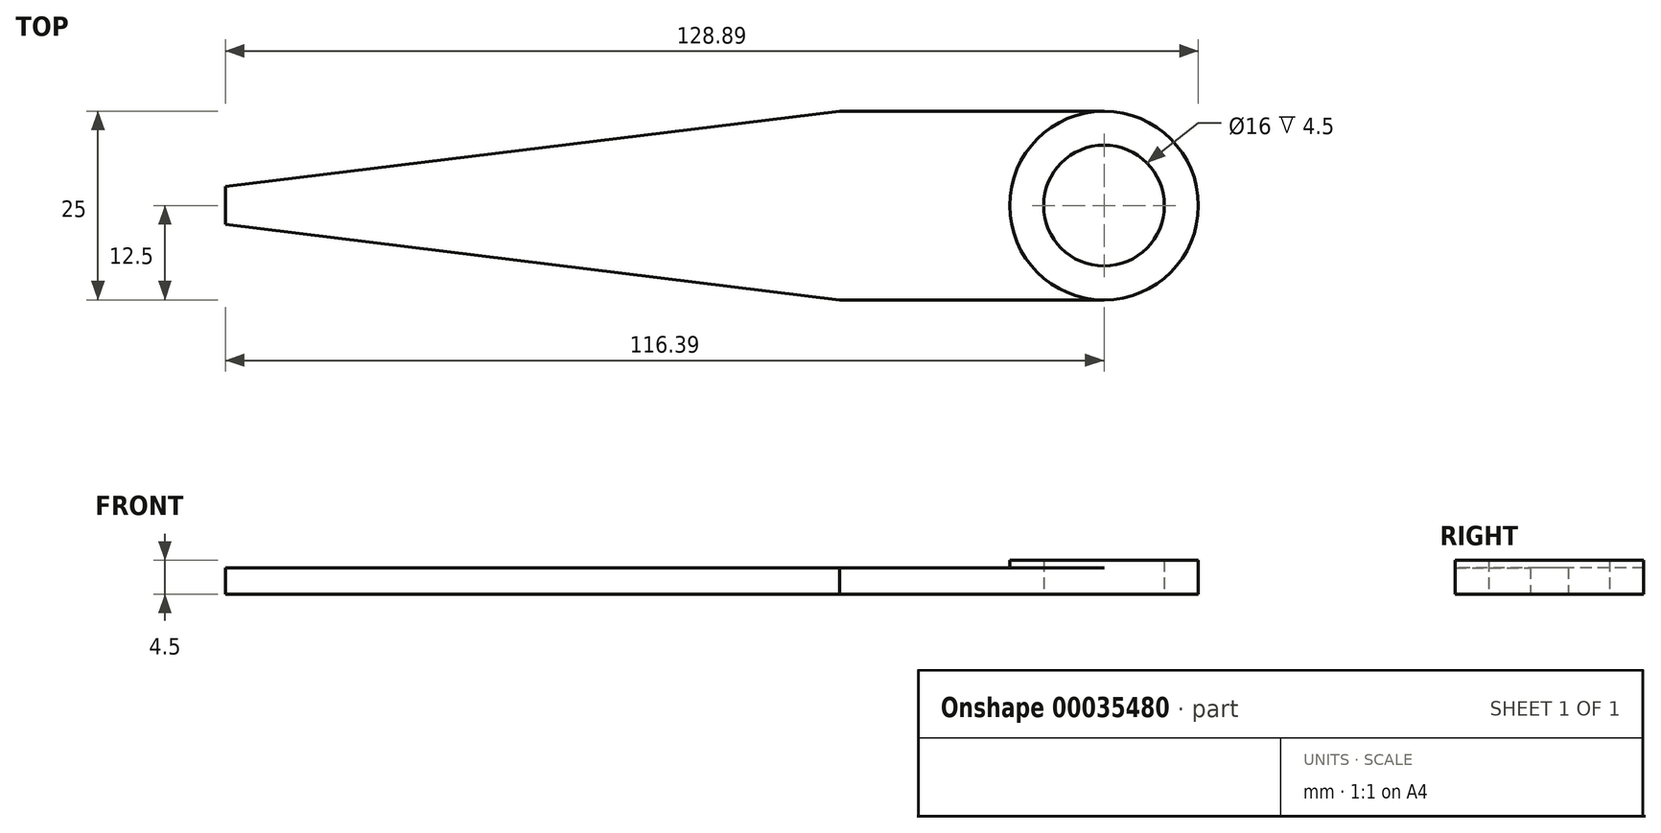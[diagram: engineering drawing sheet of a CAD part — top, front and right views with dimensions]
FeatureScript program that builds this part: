
annotation { "Feature Type Name" : "Feature", "Feature Type Description" : "" }
export const myFeature = defineFeature(function(context is Context, id is Id, definition is map)
    precondition{}
    {
        {
            var Q0;
            Q0=qCreatedBy(makeId("Top.planeOp"),FACE);
            var sketch = newSketch(context, id + "F0", { "sketchPlane" : qUnion([Q0])});
            skCircle(sketch, "E0", {"center": v(0, 0) * mm, "radius": 8 * mm});
            skCircle(sketch, "E1", {"center": v(0, 0) * mm, "radius": 12.5 * mm});
            skLineSegment(sketch, "E2", {"start": v(-35, 12.5) * mm, "end": v(0, 12.5) * mm});
            skLineSegment(sketch, "E3", {"start": v(-35, -12.5) * mm, "end": v(0, -12.5) * mm});
            skLineSegment(sketch, "E4", {"start": v(-35, 12.5) * mm, "end": v(-105.9, 12.5) * mm, "construction": true});
            skLineSegment(sketch, "E5", {"start": v(-35, 12.5) * mm, "end": v(-116.39, 2.5) * mm});
            skLineSegment(sketch, "E6", {"start": v(-35, -12.5) * mm, "end": v(-125, -12.5) * mm, "construction": true});
            skLineSegment(sketch, "E7", {"start": v(-35, -12.5) * mm, "end": v(-116.39, -2.5) * mm});
            skLineSegment(sketch, "E8", {"start": v(-116.39, 2.5) * mm, "end": v(-116.39, -2.5) * mm});
            skSolve(sketch);
        }
        {
            var Q0;
            Q0 = qSketchRegion(id + "F0", true);
            extrude(context, id + "F1", {"entities" : qUnion([Q0]), "depth" : 3.5 * mm});
        }
        {
            var Q0;
            Q0=makeQuery(id+"F1.opExtrude","CAP_FACE",FACE,{"disambiguationData":[OSD([sQuery(id+"F0.wireOp",EDGE,"E0"),sQuery(id+"F0.wireOp",EDGE,"E1"),sQuery(id+"F0.wireOp",EDGE,"E2"),sQuery(id+"F0.wireOp",EDGE,"E3"),sQuery(id+"F0.wireOp",EDGE,"E5"),sQuery(id+"F0.wireOp",EDGE,"E7"),sQuery(id+"F0.wireOp",EDGE,"E8")])],"isStart":false});
            var sketch = newSketch(context, id + "F2", { "sketchPlane" : qUnion([Q0])});
            skCircle(sketch, "E9", {"center": v(0, 0) * mm, "radius": 12.5 * mm});
            skCircle(sketch, "E10", {"center": v(0, 0) * mm, "radius": 8 * mm});
            skSolve(sketch);
        }
        {
            var Q0;
            Q0=makeQuery(id+"F2.imprint","IMPRINT",FACE,{"disambiguationData":[TD([[makeQuery(id+"F2.imprint","IMPRINT",EDGE,{"derivedFrom":sQuery(id+"F2.wireOp",EDGE,"E10")}),-1.0]])]});
            extrude(context, id + "F3", {"entities" : qUnion([Q0]), "operationType" : NewBodyOperationType.ADD, "depth" : 1 * mm});
        }
    });
